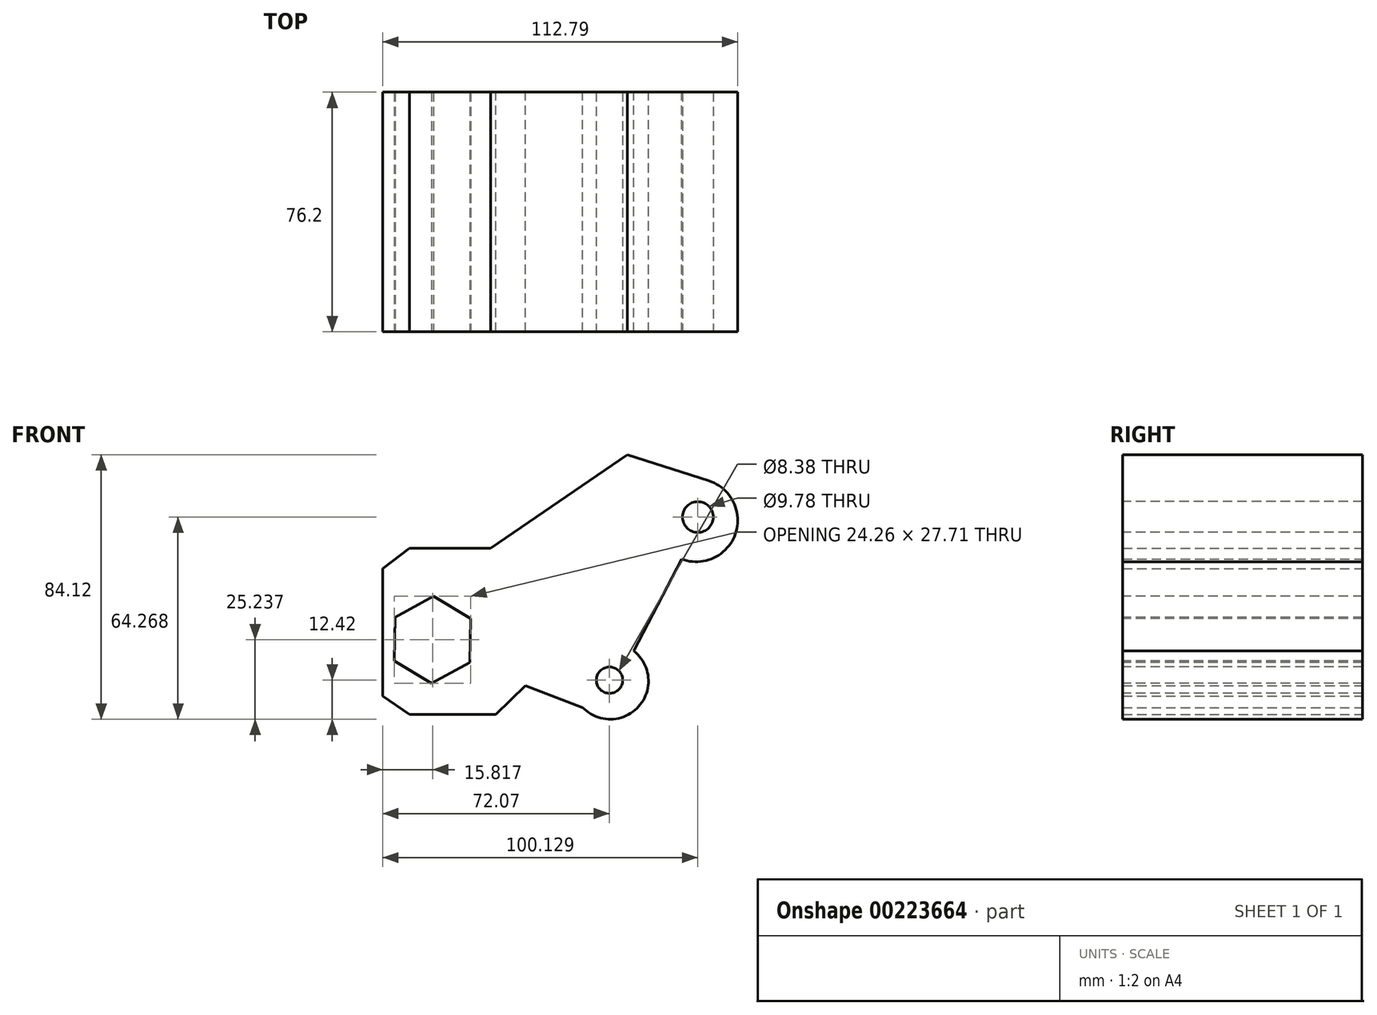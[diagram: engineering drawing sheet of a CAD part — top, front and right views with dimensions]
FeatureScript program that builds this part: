
annotation { "Feature Type Name" : "Feature", "Feature Type Description" : "" }
export const myFeature = defineFeature(function(context is Context, id is Id, definition is map)
    precondition{}
    {
        {
            var Q0;
            Q0=qCreatedBy(makeId("Front.planeOp"),FACE);
            var sketch = newSketch(context, id + "F0", { "sketchPlane" : qUnion([Q0])});
            skLineSegment(sketch, "E0", {"start": v(-62.05, 22.98) * mm, "end": v(-53.52, 29.48) * mm});
            skLineSegment(sketch, "E1", {"start": v(-62.05, 22.98) * mm, "end": v(-62.05, -17.52) * mm});
            skLineSegment(sketch, "E2", {"start": v(-62.05, -17.52) * mm, "end": v(-53.52, -23.4) * mm});
            skLineSegment(sketch, "E3", {"start": v(-53.52, 29.48) * mm, "end": v(-27.7, 29.48) * mm});
            skLineSegment(sketch, "E4", {"start": v(-27.7, 29.48) * mm, "end": v(15.72, 59.21) * mm});
            skLineSegment(sketch, "E5", {"start": v(15.72, 59.21) * mm, "end": v(41.6, 50.87) * mm});
            skLineSegment(sketch, "E6", {"start": v(17.7, -3.22) * mm, "end": v(32.9, 25.97) * mm});
            skLineSegment(sketch, "E7", {"start": v(-53.52, -23.4) * mm, "end": v(-26.11, -23.4) * mm});
            skLineSegment(sketch, "E8", {"start": v(-26.11, -23.4) * mm, "end": v(-16.77, -14.27) * mm});
            skLineSegment(sketch, "E9", {"start": v(-16.77, -14.27) * mm, "end": v(1.5, -21.18) * mm});
            skArc(sketch, "E10", {"start": v(1.5, -21.18) * mm, "mid": v(19.26, -20.91) * mm, "end": v(17.7, -3.22) * mm});
            skArc(sketch, "E11", {"start": v(32.9, 25.97) * mm, "mid": v(50, 33.97) * mm, "end": v(41.6, 50.87) * mm});
            skSolve(sketch);
        }
        {
            var Q0;
            Q0=makeQuery(id+"F0.imprint","IMPRINT",FACE,{"disambiguationData":[TD([[makeQuery(id+"F0.imprint","IMPRINT",EDGE,{"derivedFrom":sQuery(id+"F0.wireOp",EDGE,"E0")}),-1.0]])]});
            var sketch = newSketch(context, id + "F1", { "sketchPlane" : qUnion([Q0])});
            skCircle(sketch, "E12", {"center": v(10.02, -12.5) * mm, "radius": 4.2 * mm});
            skCircle(sketch, "E13", {"center": v(38.08, 39.36) * mm, "radius": 4.89 * mm});
            skCircle(sketch, "E14.cCircle", {"center": v(-46.23, 0.33) * mm, "radius": 12 * mm, "construction": true});
            skLineSegment(sketch, "E14.0", {"start": v(-34.36, -6.83) * mm, "end": v(-46.5, -13.53) * mm});
            skLineSegment(sketch, "E14.1", {"start": v(-46.5, -13.53) * mm, "end": v(-58.37, -6.38) * mm});
            skLineSegment(sketch, "E14.2", {"start": v(-58.37, -6.38) * mm, "end": v(-58.1, 7.48) * mm});
            skLineSegment(sketch, "E14.3", {"start": v(-58.1, 7.48) * mm, "end": v(-45.97, 14.18) * mm});
            skLineSegment(sketch, "E14.4", {"start": v(-45.97, 14.18) * mm, "end": v(-34.1, 7.03) * mm});
            skLineSegment(sketch, "E14.5", {"start": v(-34.1, 7.03) * mm, "end": v(-34.36, -6.83) * mm});
            skSolve(sketch);
        }
        {
            var Q0;
            Q0 = qSketchRegion(id + "F0", true);
            extrude(context, id + "F2", {"entities" : qUnion([Q0]), "endBound" : BoundingType.SYMMETRIC, "depth" : 76.2 * mm});
        }
        {
            var Q0;
            Q0 = qSketchRegion(id + "F1", true);
            var Q1;
            Q1=makeQuery(id+"F2.opExtrude","CAP_FACE",FACE,{"disambiguationData":[OSD([sQuery(id+"F0.wireOp",EDGE,"E0"),sQuery(id+"F0.wireOp",EDGE,"E1"),sQuery(id+"F0.wireOp",EDGE,"E2"),sQuery(id+"F0.wireOp",EDGE,"E3"),sQuery(id+"F0.wireOp",EDGE,"E4"),sQuery(id+"F0.wireOp",EDGE,"E5"),sQuery(id+"F0.wireOp",EDGE,"E6"),sQuery(id+"F0.wireOp",EDGE,"E7"),sQuery(id+"F0.wireOp",EDGE,"E8"),sQuery(id+"F0.wireOp",EDGE,"E9"),sQuery(id+"F0.wireOp",EDGE,"E10"),sQuery(id+"F0.wireOp",EDGE,"E11")])],"isStart":true});
            extrude(context, id + "F3", {"entities" : qUnion([Q0]), "operationType" : NewBodyOperationType.REMOVE, "endBound" : BoundingType.SYMMETRIC, "oppositeDirection" : true, "endBoundEntityFace" : qUnion([Q1]), "depth" : 76.2 * mm});
        }
    });
